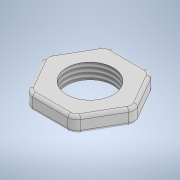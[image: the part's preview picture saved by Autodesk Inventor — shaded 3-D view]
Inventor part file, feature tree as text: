
AUTODESK INVENTOR PART (.ipt)
format: ipt  version: 2021 (Build 250183000, 183)  size: 163,328 bytes
history: native  units: mm
features: extrude x1, fillet x1, thread x1, sketch x1
ambient origin geometry x8: Origin, YZ Plane, XZ Plane, XY Plane, X Axis, Y Axis, Z Axis, Center Point
bodies: Solid1 (feature_tree)
feature tree (4):
  extrude  "Extrusion1"  Depth=1.5mm
  fillet  "Fillet1"  Radius=1.5mm
  thread  "Thread1"  [1 undecoded]
  sketch  "Sketch1"  dims[d0=12.9mm d1=1.5mm d2=1.5mm d3=7.6mm d4=2.5mm d5=0.0mm d6=0.5mm d7=12.5mm d8=0.0mm]
note: 1 required parameter value undecoded (feature->parameter linkage not recoverable at this tier; creation-order binding heuristic only, values carry confidence <= 0.55)
